# Revit family: 304_Cim727OTS-_
name_source: partatom
category: Pipe Accessories
revit_build: Autodesk Revit 2017 (Build: 20160225_1515(x64)
units: mm (PartAtom-declared; Revit-internal decimal feet)

## family parameters
Always vertical = Yes
Cut with Voids When Loaded = No
Part Type = Valve - Breaks Into
Round Connector Dimension = Use Diameter
Shared = No
Work Plane-Based = No

## types (7) — shared parameters
CAT0 = Yes
Description = BALANCING VALVE FOR SOLAR HEATING SYSTEMS - PN 20
L2D_Min = 3048 mm
Manufacturer = Cimberio
QmdConnectorList = 301;D;302;D
URL = www.cimberio.it
magiPartTypeId = 304
magiProductFamilyId = Cim727OTS-*
zero-valued in all types: MC_Default_elevation

## per-type parameters (varying)
| type | CenSd_R1_6 | D | D1 | DL | DL__ve | L2D | LL1 | LL2 | R1 | W2D | X | XX1 | Z |
| Cim727OTS-15 | 12 mm  [stored 0.0393701 ft] | 15 mm | 17 mm | 15 mm  [stored 0.0492126 ft] | -15 mm  [stored -0.0492126 ft] | 68 mm | 34 mm  [stored 0.111549 ft] | 38 mm  [stored 0.124672 ft] | 14 mm  [stored 0.0459318 ft] | 15 mm  [stored 0.0492126 ft] | 90 mm | 105 mm | 88 mm  [stored 0.288714 ft] |
| Cim727OTS-50 | 31 mm | 50 mm | 55 mm  [stored 0.180446 ft] | 26 mm | -26 mm | 143 mm | 72 mm | 92 mm | 36 mm | 50 mm  [stored 0.164042 ft] | 142 mm | 177 mm | 177 mm |
| Cim727OTS-40 | 24 mm  [stored 0.0787402 ft] | 40 mm | 44 mm  [stored 0.144357 ft] | 21 mm | -21 mm | 116 mm | 58 mm  [stored 0.190289 ft] | 73 mm | 28 mm  [stored 0.0918635 ft] | 40 mm  [stored 0.131234 ft] | 136 mm | 165 mm | 165 mm |
| Cim727OTS-32 | 22 mm  [stored 0.0721785 ft] | 32 mm | 35 mm | 21 mm | -21 mm | 108 mm | 54 mm  [stored 0.177165 ft] | 65 mm | 26 mm | 32 mm  [stored 0.104987 ft] | 102 mm | 128 mm | 128 mm |
| Cim727OTS-25 | 17 mm | 25 mm | 28 mm  [stored 0.0918635 ft] | 19 mm  [stored 0.062336 ft] | -19 mm  [stored -0.062336 ft] | 91 mm | 46 mm | 53 mm | 20 mm  [stored 0.0656168 ft] | 25 mm  [stored 0.082021 ft] | 99 mm | 119 mm | 119 mm |
| Cim727OTS-20 | 14 mm  [stored 0.0459318 ft] | 20 mm | 22 mm  [stored 0.0721785 ft] | 16 mm | -16 mm | 77 mm | 39 mm | 44 mm  [stored 0.144357 ft] | 17 mm | 20 mm  [stored 0.0656168 ft] | 105 mm | 125 mm | 105 mm |
| Cim727OTS-15L | 12 mm  [stored 0.0393701 ft] | 15 mm | 17 mm | 15 mm  [stored 0.0492126 ft] | -15 mm  [stored -0.0492126 ft] | 68 mm | 34 mm  [stored 0.111549 ft] | 38 mm  [stored 0.124672 ft] | 14 mm  [stored 0.0459318 ft] | 15 mm  [stored 0.0492126 ft] | 90 mm | 105 mm | 88 mm  [stored 0.288714 ft] |

note: column(s) folded — value = type name in every type: magiProductCode, magiProductId

note: [stored X ft] marks values corroborated as IEEE doubles in the binary element streams (Revit-internal decimal feet)

## geometry (parser evidence)
native form markers: Sweep x2
no freeform markers — native parametric forms only
